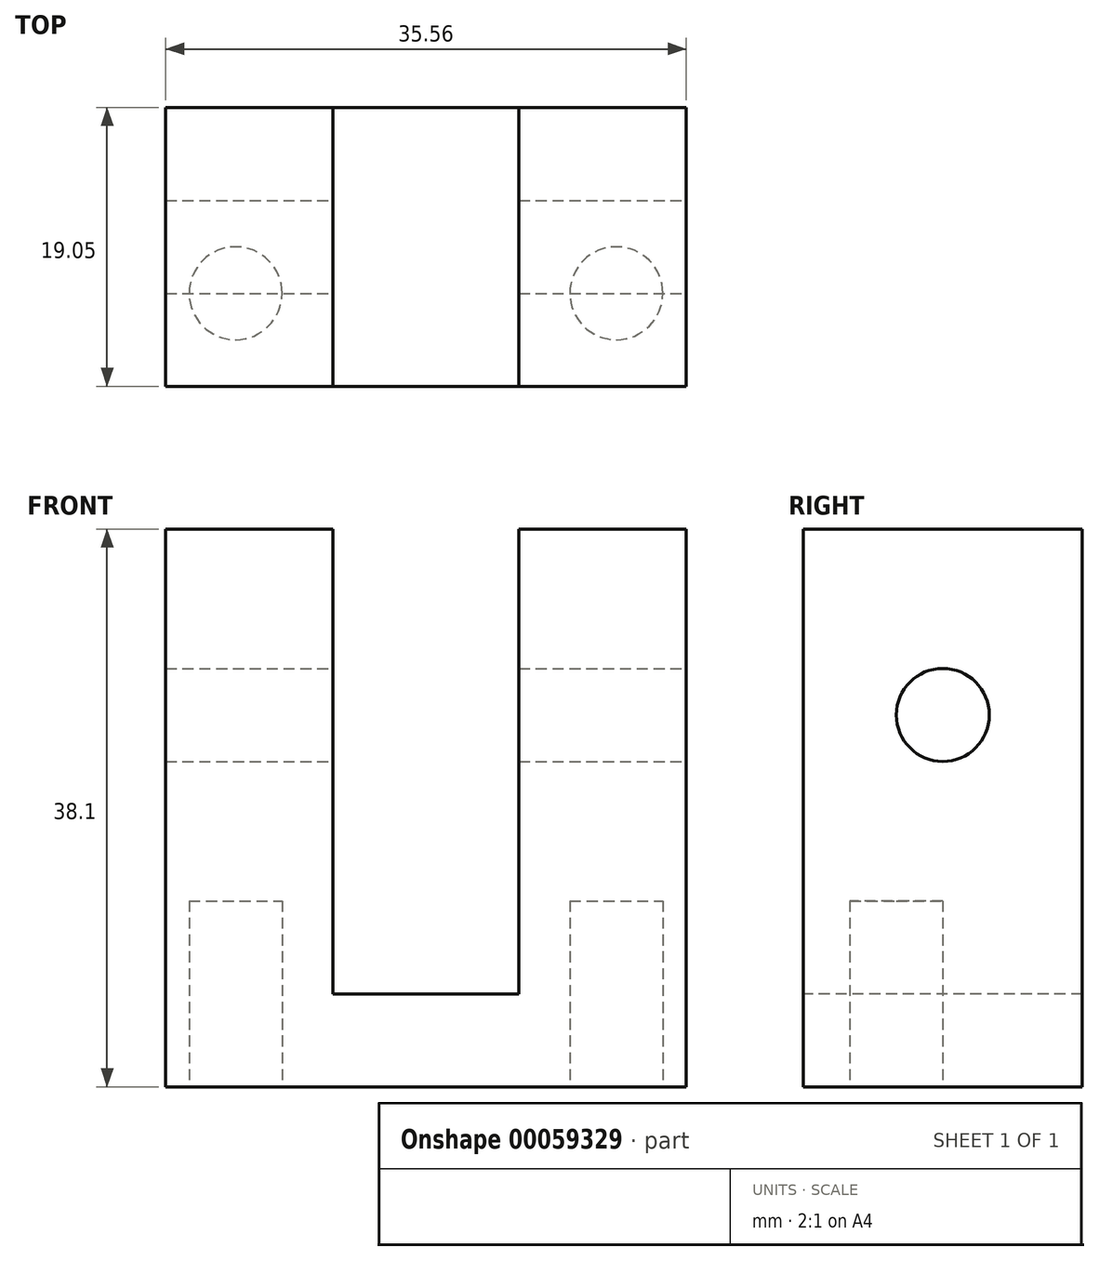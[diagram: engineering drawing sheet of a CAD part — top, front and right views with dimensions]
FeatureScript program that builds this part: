
annotation { "Feature Type Name" : "Feature", "Feature Type Description" : "" }
export const myFeature = defineFeature(function(context is Context, id is Id, definition is map)
    precondition{}
    {
        {
            var Q0;
            Q0=qCreatedBy(makeId("Front.planeOp"),FACE);
            var sketch = newSketch(context, id + "F0", { "sketchPlane" : qUnion([Q0])});
            skLineSegment(sketch, "E0.bottom", {"start": v(0, 0) * mm, "end": v(35.56, 0) * mm});
            skLineSegment(sketch, "E0.top", {"start": v(0, 38.1) * mm, "end": v(35.56, 38.1) * mm});
            skLineSegment(sketch, "E0.left", {"start": v(0, 0) * mm, "end": v(0, 38.1) * mm});
            skLineSegment(sketch, "E0.right", {"start": v(35.56, 0) * mm, "end": v(35.56, 38.1) * mm});
            skSolve(sketch);
        }
        {
            var Q0;
            Q0 = qSketchRegion(id + "F0", true);
            extrude(context, id + "F1", {"entities" : qUnion([Q0]), "depth" : 19.05 * mm});
        }
        {
            var Q0;
            Q0=makeQuery(id+"F1.opExtrude","CAP_FACE",FACE,{"disambiguationData":[OSD([sQuery(id+"F0.wireOp",EDGE,"E0.bottom"),sQuery(id+"F0.wireOp",EDGE,"E0.top"),sQuery(id+"F0.wireOp",EDGE,"E0.left"),sQuery(id+"F0.wireOp",EDGE,"E0.right")])],"isStart":false});
            var sketch = newSketch(context, id + "F2", { "sketchPlane" : qUnion([Q0])});
            skLineSegment(sketch, "E1.bottom", {"start": v(11.43, 38.1) * mm, "end": v(24.13, 38.1) * mm});
            skLineSegment(sketch, "E1.top", {"start": v(11.43, 6.35) * mm, "end": v(24.13, 6.35) * mm});
            skLineSegment(sketch, "E1.left", {"start": v(11.43, 38.1) * mm, "end": v(11.43, 6.35) * mm});
            skLineSegment(sketch, "E1.right", {"start": v(24.13, 38.1) * mm, "end": v(24.13, 6.35) * mm});
            skSolve(sketch);
        }
        {
            var Q0;
            Q0 = qSketchRegion(id + "F2", true);
            extrude(context, id + "F3", {"entities" : qUnion([Q0]), "operationType" : NewBodyOperationType.REMOVE, "oppositeDirection" : true, "depth" : 25.4 * mm});
        }
        {
            var Q0;
            Q0=makeQuery(id+"F1.opExtrude","SWEPT_FACE",FACE,{"disambiguationData":[OSD([sQuery(id+"F0.wireOp",EDGE,"E0.right")])]});
            var sketch = newSketch(context, id + "F4", { "sketchPlane" : qUnion([Q0])});
            skCircle(sketch, "E2", {"center": v(-9.53, 25.4) * mm, "radius": 3.18 * mm});
            skSolve(sketch);
        }
        {
            var Q0;
            Q0=makeQuery(id+"F4.imprint","IMPRINT",FACE,{"disambiguationData":[TD([[makeQuery(id+"F4.imprint","IMPRINT",EDGE,{"derivedFrom":sQuery(id+"F4.wireOp",EDGE,"E2")}),1.0]])]});
            extrude(context, id + "F5", {"entities" : qUnion([Q0]), "operationType" : NewBodyOperationType.REMOVE, "endBound" : BoundingType.THROUGH_ALL, "oppositeDirection" : true, "depth" : 25.4 * mm});
        }
        {
            var Q0;
            Q0=makeQuery(id+"F1.opExtrude","SWEPT_FACE",FACE,{"disambiguationData":[OSD([sQuery(id+"F0.wireOp",EDGE,"E0.bottom")])]});
            var sketch = newSketch(context, id + "F6", { "sketchPlane" : qUnion([Q0])});
            skCircle(sketch, "E3", {"center": v(4.78, 12.7) * mm, "radius": 3.18 * mm});
            skCircle(sketch, "E4", {"center": v(30.78, 12.7) * mm, "radius": 3.18 * mm});
            skSolve(sketch);
        }
        {
            var Q0;
            Q0 = qSketchRegion(id + "F6", true);
            extrude(context, id + "F7", {"entities" : qUnion([Q0]), "operationType" : NewBodyOperationType.REMOVE, "oppositeDirection" : true, "depth" : 12.7 * mm});
        }
    });
